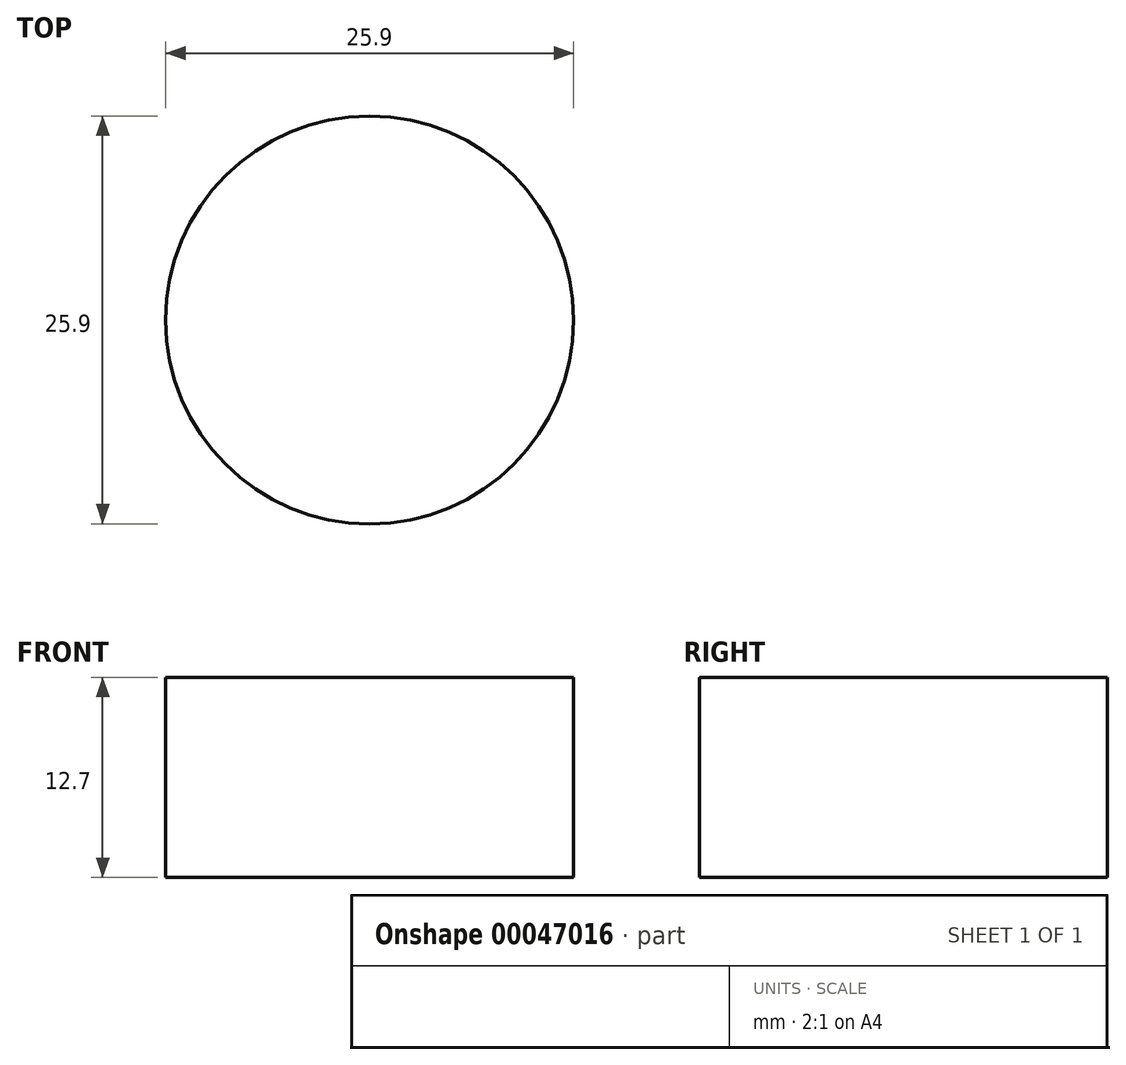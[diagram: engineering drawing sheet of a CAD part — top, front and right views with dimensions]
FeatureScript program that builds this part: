
annotation { "Feature Type Name" : "Feature", "Feature Type Description" : "" }
export const myFeature = defineFeature(function(context is Context, id is Id, definition is map)
    precondition{}
    {
        {
            var Q0;
            Q0=qCreatedBy(makeId("Top.planeOp"),FACE);
            var sketch = newSketch(context, id + "F0", { "sketchPlane" : qUnion([Q0])});
            skCircle(sketch, "E0", {"center": v(0, 0) * mm, "radius": 11.68 * mm, "construction": true});
            skCircle(sketch, "E1.0", {"center": v(0, 0) * mm, "radius": 12.95 * mm});
            skSolve(sketch);
        }
        {
            var Q0;
            Q0=makeQuery(id+"F0.imprint","IMPRINT",FACE,{"disambiguationData":[TD([[makeQuery(id+"F0.imprint","IMPRINT",EDGE,{"derivedFrom":sQuery(id+"F0.wireOp",EDGE,"E1.0")}),1.0]])]});
            extrude(context, id + "F1", {"entities" : qUnion([Q0]), "depth" : 12.7 * mm});
        }
    });
